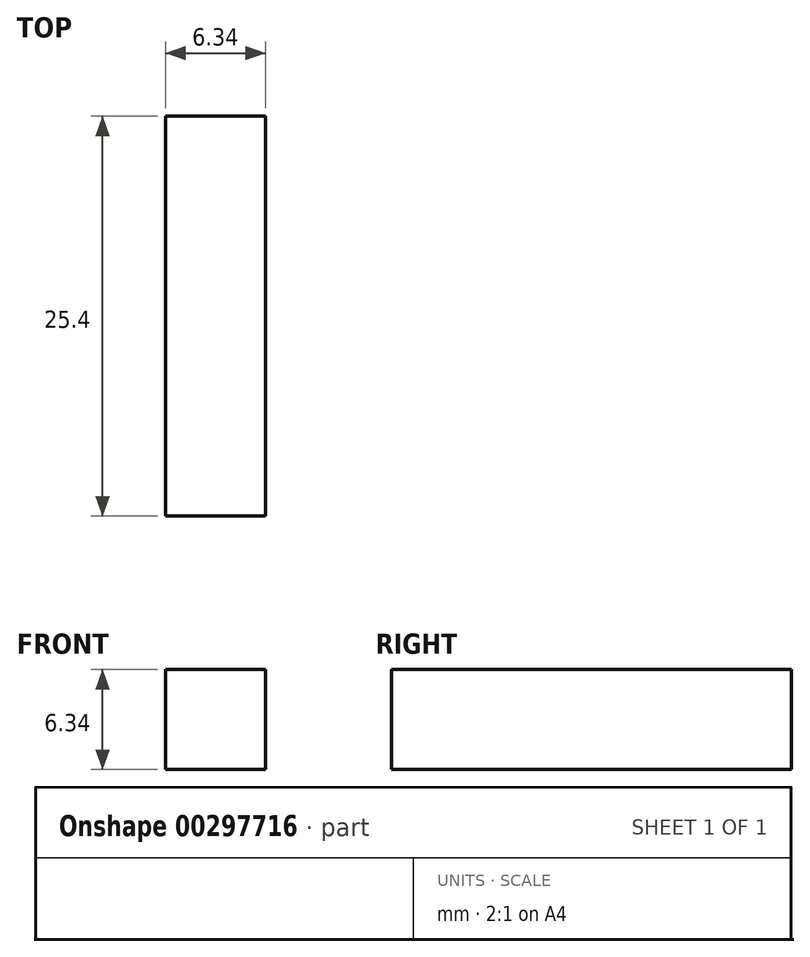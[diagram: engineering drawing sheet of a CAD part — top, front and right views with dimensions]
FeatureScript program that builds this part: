
annotation { "Feature Type Name" : "Feature", "Feature Type Description" : "" }
export const myFeature = defineFeature(function(context is Context, id is Id, definition is map)
    precondition{}
    {
        {
            var Q0;
            Q0=qCreatedBy(makeId("Front.planeOp"),FACE);
            var sketch = newSketch(context, id + "F0", { "sketchPlane" : qUnion([Q0])});
            skLineSegment(sketch, "E0.bottom", {"start": v(3.18, 3.18) * mm, "end": v(-3.17, 3.18) * mm});
            skLineSegment(sketch, "E0.top", {"start": v(3.18, -3.18) * mm, "end": v(-3.18, -3.18) * mm});
            skLineSegment(sketch, "E0.left", {"start": v(3.18, 3.17) * mm, "end": v(3.18, -3.18) * mm});
            skLineSegment(sketch, "E0.right", {"start": v(-3.17, 3.18) * mm, "end": v(-3.18, -3.17) * mm});
            skPoint(sketch, "E0.middle", {"position": v(0, 0) * mm});
            skSolve(sketch);
        }
        {
            var Q0;
            Q0 = qSketchRegion(id + "F0", true);
            extrude(context, id + "F1", {"entities" : qUnion([Q0]), "depth" : 25.4 * mm});
        }
    });
